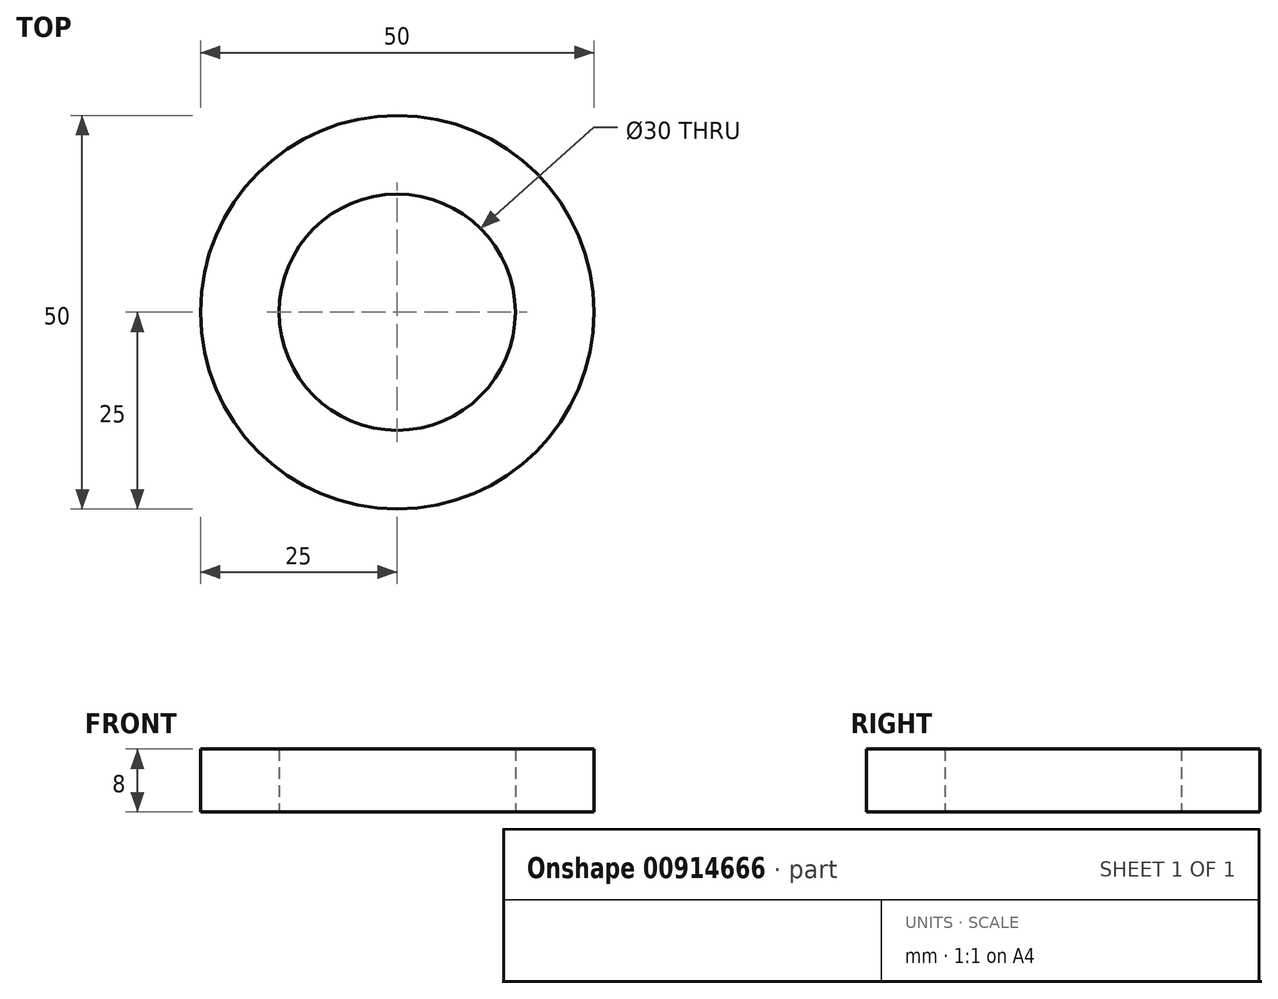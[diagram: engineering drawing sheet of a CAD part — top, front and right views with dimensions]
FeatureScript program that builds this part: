
annotation { "Feature Type Name" : "Feature", "Feature Type Description" : "" }
export const myFeature = defineFeature(function(context is Context, id is Id, definition is map)
    precondition{}
    {
        {
            var Q0;
            Q0=qCreatedBy(makeId("Top.planeOp"),FACE);
            var sketch = newSketch(context, id + "F0", { "sketchPlane" : qUnion([Q0])});
            skPoint(sketch, "E0", {"position": v(0, 0) * mm});
            skCircle(sketch, "E1", {"center": v(0, 0) * mm, "radius": 15 * mm});
            skCircle(sketch, "E2", {"center": v(0, 0) * mm, "radius": 25 * mm});
            skSolve(sketch);
        }
        {
            var Q0;
            Q0=makeQuery(id+"F0.imprint","IMPRINT",FACE,{"disambiguationData":[TD([[makeQuery(id+"F0.imprint","IMPRINT",EDGE,{"derivedFrom":sQuery(id+"F0.wireOp",EDGE,"E1")}),-1.0]])]});
            extrude(context, id + "F1", {"entities" : qUnion([Q0]), "depth" : 8 * mm, "offsetDistance" : 25 * mm});
        }
    });
